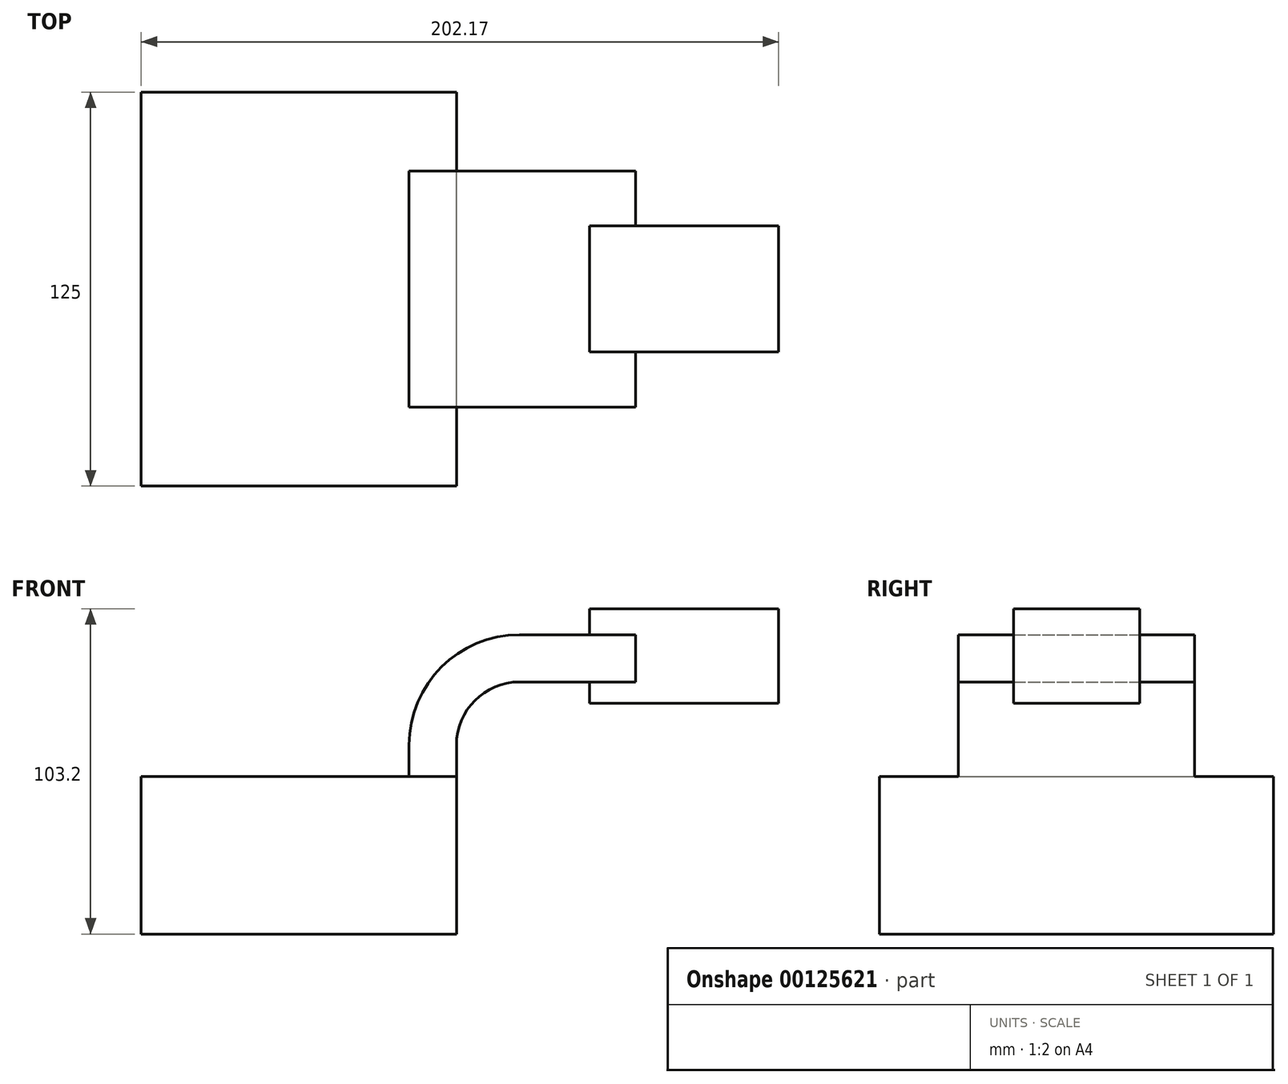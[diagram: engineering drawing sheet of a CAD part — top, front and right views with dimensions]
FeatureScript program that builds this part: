
annotation { "Feature Type Name" : "Feature", "Feature Type Description" : "" }
export const myFeature = defineFeature(function(context is Context, id is Id, definition is map)
    precondition{}
    {
        {
            var Q0;
            Q0=qCreatedBy(makeId("Front.planeOp"),FACE);
            var sketch = newSketch(context, id + "F0", { "sketchPlane" : qUnion([Q0])});
            skLineSegment(sketch, "E0.bottom", {"start": v(-50, -25) * mm, "end": v(50, -25) * mm});
            skLineSegment(sketch, "E0.top", {"start": v(-50, 25) * mm, "end": v(50, 25) * mm});
            skLineSegment(sketch, "E0.left", {"start": v(-50, -25) * mm, "end": v(-50, 25) * mm});
            skLineSegment(sketch, "E0.right", {"start": v(50, -25) * mm, "end": v(50, 25) * mm});
            skPoint(sketch, "E0.middle", {"position": v(0, 0) * mm});
            skLineSegment(sketch, "E1.bottom", {"start": v(92.17, 48.2) * mm, "end": v(152.17, 48.2) * mm});
            skLineSegment(sketch, "E1.top", {"start": v(92.17, 78.2) * mm, "end": v(152.17, 78.2) * mm});
            skLineSegment(sketch, "E1.left", {"start": v(92.17, 48.2) * mm, "end": v(92.17, 78.2) * mm});
            skLineSegment(sketch, "E1.right", {"start": v(152.17, 48.2) * mm, "end": v(152.17, 78.2) * mm});
            skPoint(sketch, "E1.middle", {"position": v(122.17, 63.2) * mm});
            skLineSegment(sketch, "E2", {"start": v(50, 25) * mm, "end": v(50, 35) * mm});
            skArc(sketch, "E3", {"start": v(50, 35) * mm, "mid": v(55.86, 49.14) * mm, "end": v(70, 55) * mm});
            skLineSegment(sketch, "E4", {"start": v(70, 55) * mm, "end": v(106.88, 55) * mm});
            skLineSegment(sketch, "E5.0", {"start": v(70, 70) * mm, "end": v(106.88, 70) * mm});
            skArc(sketch, "E5.1", {"start": v(35, 35) * mm, "mid": v(45.25, 59.75) * mm, "end": v(70, 70) * mm});
            skLineSegment(sketch, "E5.2", {"start": v(35, 25) * mm, "end": v(35, 35) * mm});
            skLineSegment(sketch, "E6", {"start": v(106.88, 55) * mm, "end": v(106.88, 48.2) * mm});
            skLineSegment(sketch, "E7", {"start": v(106.88, 55) * mm, "end": v(106.88, 78.2) * mm});
            skFitSpline(sketch, "E8", {"points": [v(-50, 25) * mm, v(92.17, 78.2) * mm], "startDerivative": vector(137.32, 137.2) * mm, "endDerivative": vector(203.75, 10.2) * mm});
            skLineSegment(sketch, "E9", {"start": v(137.27, 48.2) * mm, "end": v(50, -25) * mm});
            skLineSegment(sketch, "E10", {"start": v(127.82, 78.2) * mm, "end": v(127.82, 84.95) * mm});
            skSolve(sketch);
        }
        {
            var Q0;
            Q0=makeQuery(id+"F0.imprint","IMPRINT",FACE,{"disambiguationData":[TD([[makeQuery(id+"F0.imprint","IMPRINT",EDGE,{"derivedFrom":sQuery(id+"F0.wireOp",EDGE,"E0.bottom")}),1.0]])]});
            extrude(context, id + "F1", {"entities" : qUnion([Q0]), "endBound" : BoundingType.SYMMETRIC, "depth" : 125 * mm});
        }
        {
            var Q0;
            {var subQ0=sQuery(id+"F0.wireOp",EDGE,"E4");var subQ1=sQuery(id+"F0.wireOp",EDGE,"E1.left");var subQ2=makeQuery(id+"F0.imprint","INTERSECT",VERTEX,{"derivedFrom":[subQ1,subQ0]});Q0=makeQuery(id+"F0.imprint","IMPRINT",FACE,{"disambiguationData":[TD([[makeQuery(id+"F0.imprint","IMPRINT",EDGE,{"disambiguationData":[TD([[subQ2,-1.0]])],"derivedFrom":subQ1}),-1.0]])]});}
            var Q1;
            {var subQ1=sQuery(id+"F0.wireOp",EDGE,"E2");Q1=makeQuery(id+"F0.imprint","IMPRINT",FACE,{"disambiguationData":[TD([[makeQuery(id+"F0.imprint","IMPRINT",EDGE,{"derivedFrom":subQ1}),1.0]])]});}
            extrude(context, id + "F2", {"entities" : qUnion([Q0, Q1]), "operationType" : NewBodyOperationType.ADD, "endBound" : BoundingType.SYMMETRIC, "depth" : 75 * mm});
        }
        {
            var Q0;
            {var subQ0=sQuery(id+"F0.wireOp",EDGE,"E5.1");Q0=makeQuery(id+"F0.imprint","IMPRINT",FACE,{"disambiguationData":[TD([[makeQuery(id+"F0.imprint","IMPRINT",EDGE,{"derivedFrom":subQ0}),1.0]])]});}
            var Q1;
            {var subQ0=sQuery(id+"F0.wireOp",EDGE,"E1.right");Q1=makeQuery(id+"F0.imprint","IMPRINT",FACE,{"disambiguationData":[TD([[makeQuery(id+"F0.imprint","IMPRINT",EDGE,{"derivedFrom":subQ0}),1.0]])]});}
            var Q2;
            {var subQ3=sQuery(id+"F0.wireOp",EDGE,"E6");Q2=makeQuery(id+"F0.imprint","IMPRINT",FACE,{"disambiguationData":[TD([[makeQuery(id+"F0.imprint","IMPRINT",EDGE,{"derivedFrom":subQ3}),-1.0]])]});}
            var Q3;
            {var subQ3=sQuery(id+"F0.wireOp",EDGE,"E7");var subQ5=sQuery(id+"F0.wireOp",EDGE,"E5.0");var subQ7=makeQuery(id+"F0.imprint","INTERSECT",VERTEX,{"derivedFrom":[subQ5,subQ3]});Q3=makeQuery(id+"F0.imprint","IMPRINT",FACE,{"disambiguationData":[TD([[makeQuery(id+"F0.imprint","IMPRINT",EDGE,{"disambiguationData":[TD([[subQ7,1.0]])],"derivedFrom":subQ5}),1.0]])]});}
            extrude(context, id + "F3", {"entities" : qUnion([Q0, Q1, Q2, Q3]), "operationType" : NewBodyOperationType.ADD, "endBound" : BoundingType.SYMMETRIC, "depth" : 40 * mm});
        }
    });
